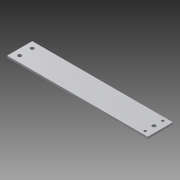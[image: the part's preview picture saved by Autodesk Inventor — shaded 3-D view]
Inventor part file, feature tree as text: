
AUTODESK INVENTOR PART (.ipt)
format: ipt  version: 2015 (Build 190159000, 159)  size: 111,616 bytes
history: native  units: mm
features: sketch x4, hole x3, other x1, extrude x1
ambient origin geometry x8: Origin, YZ Plane, XZ Plane, XY Plane, X Axis, Y Axis, Z Axis, Center Point
bodies: Body1 (feature_tree)
feature tree (9):
  other  "ソリッド1"
  extrude  "押し出し1"  Depth=112.0mm
  hole  "穴1"  [1 undecoded]
  hole  "穴2"  [1 undecoded]
  hole  "穴3"  [1 undecoded]
  sketch  "スケッチ1"
  sketch  "スケッチ3"
  sketch  "スケッチ4"
  sketch  "スケッチ5"
note: 3 required parameter values undecoded (feature->parameter linkage not recoverable at this tier; creation-order binding heuristic only, values carry confidence <= 0.55)
